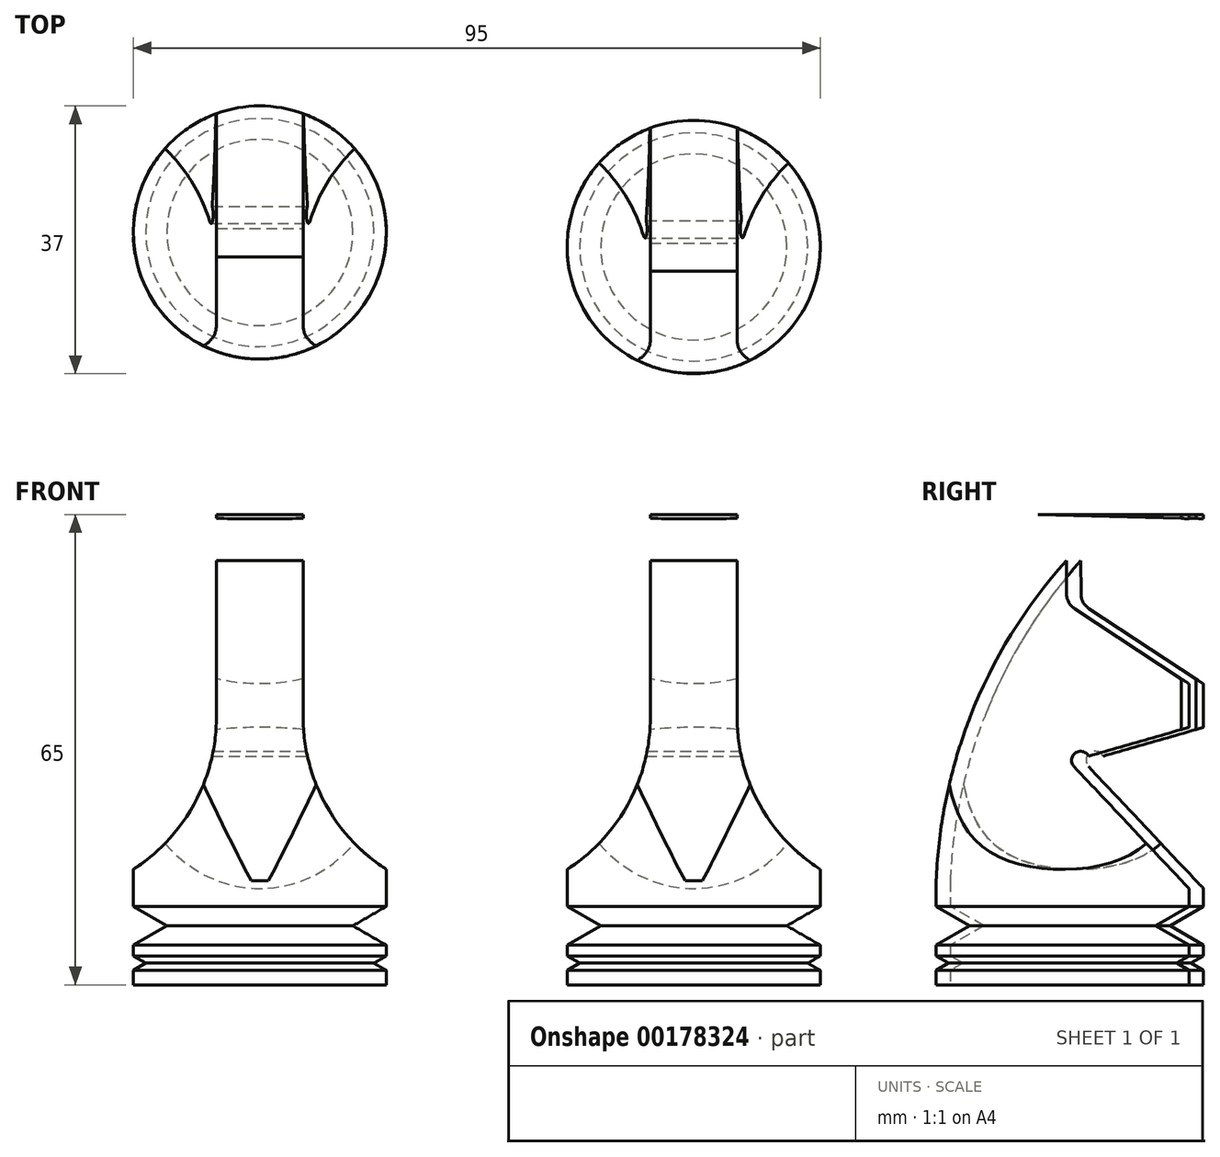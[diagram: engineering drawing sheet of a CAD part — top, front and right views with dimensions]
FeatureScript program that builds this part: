
annotation { "Feature Type Name" : "Feature", "Feature Type Description" : "" }
export const myFeature = defineFeature(function(context is Context, id is Id, definition is map)
    precondition{}
    {
        {
            var Q0;
            Q0=qCreatedBy(makeId("Top.planeOp"),FACE);
            var sketch = newSketch(context, id + "F0", { "sketchPlane" : qUnion([Q0])});
            skCircle(sketch, "E0", {"center": v(0, 0) * mm, "radius": 17.5 * mm});
            skSolve(sketch);
        }
        {
            var Q0;
            Q0=makeQuery(id+"F0.imprint","IMPRINT",FACE,{"disambiguationData":[TD([[makeQuery(id+"F0.imprint","IMPRINT",EDGE,{"derivedFrom":sQuery(id+"F0.wireOp",EDGE,"E0")}),1.0]])]});
            extrude(context, id + "F1", {"entities" : qUnion([Q0]), "depth" : 65 * mm});
        }
        {
            var Q0;
            Q0=qCreatedBy(makeId("Front.planeOp"),FACE);
            var sketch = newSketch(context, id + "F2", { "sketchPlane" : qUnion([Q0])});
            skCircle(sketch, "E1", {"center": v(31, 37) * mm, "radius": 25 * mm});
            skLineSegment(sketch, "E2", {"start": v(6, 37) * mm, "end": v(6, 65) * mm});
            skLineSegment(sketch, "E3", {"start": v(-6, 37) * mm, "end": v(-6, 65) * mm});
            skCircle(sketch, "E4", {"center": v(-31, 37) * mm, "radius": 25 * mm});
            skLineSegment(sketch, "E5", {"start": v(60.79, 12) * mm, "end": v(-67.6, 12) * mm, "construction": true});
            skLineSegment(sketch, "E6", {"start": v(-6, 65) * mm, "end": v(-32.07, 65) * mm});
            skLineSegment(sketch, "E7", {"start": v(-32.07, 65) * mm, "end": v(-32.07, 61.98) * mm});
            skLineSegment(sketch, "E8", {"start": v(6, 65) * mm, "end": v(30.35, 65) * mm});
            skLineSegment(sketch, "E9", {"start": v(30.35, 65) * mm, "end": v(30.35, 61.98) * mm});
            skSolve(sketch);
        }
        {
            var Q0;
            Q0=qCreatedBy(makeId("Right.planeOp"),FACE);
            var sketch = newSketch(context, id + "F3", { "sketchPlane" : qUnion([Q0])});
            skLineSegment(sketch, "E10", {"start": v(17.5, 41.6) * mm, "end": v(1.67, 52) * mm});
            skLineSegment(sketch, "E11", {"start": v(17.5, 41.6) * mm, "end": v(17.5, 35.6) * mm});
            skLineSegment(sketch, "E12", {"start": v(17.5, 35.6) * mm, "end": v(3.61, 31.61) * mm});
            skLineSegment(sketch, "E13", {"start": v(-17.46, 14.39) * mm, "end": v(-43.14, 14.39) * mm});
            skLineSegment(sketch, "E14", {"start": v(32.2, 59.9) * mm, "end": v(30.53, 59.9) * mm});
            skLineSegment(sketch, "E15", {"start": v(5.17, 69.26) * mm, "end": v(3.68, 64.81) * mm});
            skLineSegment(sketch, "E16.0", {"start": v(32.2, 54.9) * mm, "end": v(-29.95, 54.85) * mm, "construction": true});
            skArc(sketch, "E17.filletArc", {"start": v(0.55, 54.08) * mm, "mid": v(0.85, 52.9) * mm, "end": v(1.67, 52) * mm});
            skArc(sketch, "E18", {"start": v(0.54, 58.64) * mm, "mid": v(-12.35, 38.1) * mm, "end": v(-17.46, 14.39) * mm});
            skLineSegment(sketch, "E19", {"start": v(1.6, 30.18) * mm, "end": v(17.5, 13.3) * mm});
            skLineSegment(sketch, "E20", {"start": v(17.5, 13.3) * mm, "end": v(29.28, 13.3) * mm});
            skLineSegment(sketch, "E21", {"start": v(29.28, 13.3) * mm, "end": v(30.64, 64.1) * mm});
            skLineSegment(sketch, "E22", {"start": v(30.64, 64.1) * mm, "end": v(-24.12, 65.55) * mm});
            skLineSegment(sketch, "E23", {"start": v(-24.12, 65.55) * mm, "end": v(-43.14, 14.39) * mm});
            skLineSegment(sketch, "E24", {"start": v(17.5, 35.6) * mm, "end": v(17.5, 41.6) * mm});
            skLineSegment(sketch, "E25.trimOffspring", {"start": v(0.54, 58.64) * mm, "end": v(0.55, 54.08) * mm});
            skLineSegment(sketch, "E26", {"start": v(0.55, 54.08) * mm, "end": v(0.54, 58.64) * mm});
            skLineSegment(sketch, "E27.0", {"start": v(2.16, 32.24) * mm, "end": v(-2.28, 30.96) * mm});
            skArc(sketch, "E28", {"start": v(3.61, 31.61) * mm, "mid": v(1.78, 32.05) * mm, "end": v(1.6, 30.18) * mm});
            skLineSegment(sketch, "E29.top", {"start": v(0, 60) * mm, "end": v(17.5, 60) * mm});
            skLineSegment(sketch, "E29.left", {"start": v(0, 0) * mm, "end": v(0, 31.62) * mm, "construction": true});
            skLineSegment(sketch, "E30.bottom", {"start": v(0, 0) * mm, "end": v(17.5, 0) * mm, "construction": true});
            skLineSegment(sketch, "E30.left", {"start": v(0, 0) * mm, "end": v(0, 31.62) * mm});
            skLineSegment(sketch, "E30.right", {"start": v(17.5, 0) * mm, "end": v(17.5, 60) * mm});
            skLineSegment(sketch, "E31.trimOffspring", {"start": v(0, 54.88) * mm, "end": v(0, 60) * mm, "construction": true});
            skLineSegment(sketch, "E32.trimOffspring", {"start": v(0, 54.88) * mm, "end": v(0, 60) * mm});
            skLineSegment(sketch, "E33", {"start": v(0, 0) * mm, "end": v(-17.5, 0) * mm});
            skLineSegment(sketch, "E34", {"start": v(-17.5, 0) * mm, "end": v(-17.56, 62.87) * mm, "construction": true});
            skSolve(sketch);
        }
        {
            var Q0;
            Q0=qCreatedBy(makeId("Right.planeOp"),FACE);
            var sketch = newSketch(context, id + "F4", { "sketchPlane" : qUnion([Q0])});
            skLineSegment(sketch, "E35", {"start": v(-37.96, 0) * mm, "end": v(43.86, 0) * mm, "construction": true});
            skLineSegment(sketch, "E36.0", {"start": v(-46.41, 2) * mm, "end": v(35.4, 2) * mm, "construction": true});
            skLineSegment(sketch, "E37.0", {"start": v(-44.62, 4) * mm, "end": v(37.2, 4) * mm, "construction": true});
            skLineSegment(sketch, "E38", {"start": v(0, -7.58) * mm, "end": v(0, 18.55) * mm});
            skLineSegment(sketch, "E39.0", {"start": v(17.5, -7.58) * mm, "end": v(17.5, 18.55) * mm});
            skLineSegment(sketch, "E40.0", {"start": v(-17.5, -7.58) * mm, "end": v(-17.5, 18.55) * mm});
            skLineSegment(sketch, "E41.0", {"start": v(-44.62, 3) * mm, "end": v(37.2, 3) * mm, "construction": true});
            skLineSegment(sketch, "E42", {"start": v(-17.5, 2) * mm, "end": v(-15.77, 3) * mm});
            skLineSegment(sketch, "E43", {"start": v(-15.77, 3) * mm, "end": v(-17.5, 4) * mm});
            skLineSegment(sketch, "E44", {"start": v(-17.5, 5.49) * mm, "end": v(-8.3, 10.8) * mm});
            skLineSegment(sketch, "E45", {"start": v(-17.5, 10.84) * mm, "end": v(-12.87, 8.16) * mm});
            skSolve(sketch);
        }
        {
            var Q0;
            Q0 = qSketchRegion(id + "F4", true);
            var Q1;
            Q1=sQuery(id+"F4.wireOp",EDGE,"E38");
            revolve(context, id + "F5", {"operationType" : NewBodyOperationType.REMOVE, "entities" : qUnion([Q0]), "axis" : qUnion([Q1]), "revolveType" : RevolveType.FULL, "oppositeDirection" : true});
        }
        {
            var Q0;
            Q0 = qSketchRegion(id + "F3", true);
            extrude(context, id + "F6", {"entities" : qUnion([Q0]), "operationType" : NewBodyOperationType.REMOVE, "oppositeDirection" : true, "depth" : 92 * mm, "symmetric" : true});
        }
        {
            var Q0;
            Q0 = qSketchRegion(id + "F2", true);
            extrude(context, id + "F7", {"entities" : qUnion([Q0]), "operationType" : NewBodyOperationType.REMOVE, "depth" : 89 * mm, "symmetric" : true});
        }
        {
            var Q0;
            Q0=makeQuery(id+"F1.opExtrude","SWEPT_BODY",BODY,{"disambiguationData":[OSD([sQuery(id+"F0.wireOp",EDGE,"E0")])]});
            transform(context, id + "F8", {"entities" : qUnion([Q0]), "transformType" : TransformType.TRANSLATION_3D, "dx" : 0 * mm, "dy" : 0 * mm, "dz" : 0 * mm, "makeCopy" : true});
        }
        {
            var Q0;
            Q0=makeQuery(id+"F8.opPattern","COPY",BODY,{"derivedFrom":makeQuery(id+"F1.opExtrude","SWEPT_BODY",BODY,{"disambiguationData":[OSD([sQuery(id+"F0.wireOp",EDGE,"E0")])]}),"instanceName":"1"});
            deleteBodies(context, id + "F9", {"entities" : qUnion([Q0])});
        }
        {
            var Q0;
            Q0=makeQuery(id+"F1.opExtrude","SWEPT_BODY",BODY,{"disambiguationData":[OSD([sQuery(id+"F0.wireOp",EDGE,"E0")])]});
            transform(context, id + "F10", {"entities" : qUnion([Q0]), "transformType" : TransformType.TRANSLATION_3D, "dx" : 0 * mm, "dy" : 0 * mm, "dz" : 0 * mm, "makeCopy" : true});
        }
        {
            var Q0;
            Q0=makeQuery(id+"F1.opExtrude","SWEPT_BODY",BODY,{"disambiguationData":[OSD([sQuery(id+"F0.wireOp",EDGE,"E0")])]});
            transform(context, id + "F11", {"entities" : qUnion([Q0]), "transformType" : TransformType.TRANSLATION_3D, "dx" : 60 * mm, "dy" : -2 * mm, "dz" : 0 * mm, "makeCopy" : true});
        }
        {
            var Q0;
            Q0=makeQuery(id+"F10.opPattern","COPY",BODY,{"derivedFrom":makeQuery(id+"F1.opExtrude","SWEPT_BODY",BODY,{"disambiguationData":[OSD([sQuery(id+"F0.wireOp",EDGE,"E0")])]}),"instanceName":"1"});
            deleteBodies(context, id + "F12", {"entities" : qUnion([Q0])});
        }
    });
